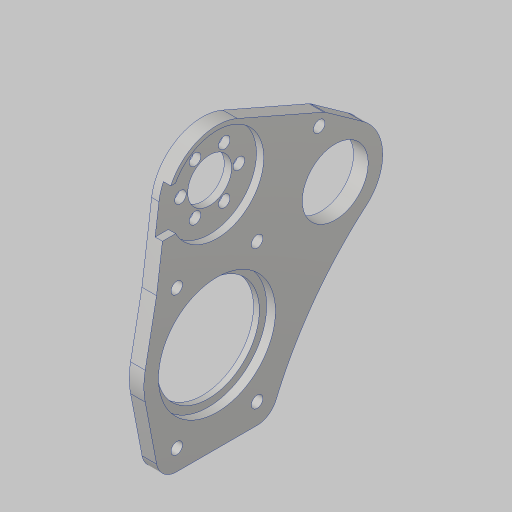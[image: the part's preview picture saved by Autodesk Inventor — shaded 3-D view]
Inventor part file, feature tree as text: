
AUTODESK INVENTOR PART (.ipt)
format: ipt  version: 2023.5 (Build 275446000, 446)  size: 250,880 bytes
history: native  units: in
note: dims shown in document units (in); Inventor stores cm internally (conversion verified against a paired STEP export)
features: sketch x5, extrude x4, hole x2, projected_geometry x1
ambient origin geometry x8: Origin, YZ Plane, XZ Plane, XY Plane, X Axis, Y Axis, Z Axis, Center Point
bodies: Solid1 (feature_tree)
feature tree (12):
  sketch  "Sketch1"  dims[d0=3.0in d1=2.2in]
  sketch  "Sketch2"  dims[d2=3.0in d3=2.375in]
  extrude  "Extrusion1"  Depth=2.2in
  hole  "Motor Mount Holes"  [1 undecoded]
  hole  "Hole3"  [1 undecoded]
  extrude  "Extrusion2"  Depth=0.201in
  extrude  "Extrusion3"  Depth=1.0in
  extrude  "Extrusion4"  Depth=0.875in TaperAngle=360.0deg
  sketch  "Sketch3"  dims[d4=1.375in d5=0.201in]
  sketch  "Sketch4"  dims[d6=0.201in d7=0.201in]
  sketch  "Sketch5"  dims[d8=0.201in d9=1.0in d12=2.3622in d14=360.0deg d16=1.125in d17=2.246in d19=2.0in d20=0.75in d23=0.25in d24=0.25in d25=0.0in d33=0.196in d34=0.75in d35=0.375in d36=0.25in d37=0.5635in d38=1.0in d39=0.8108in d41=1.1811in d43=360.0deg d45=0.375in d46=0.385in d47=0.375in d49=0.196in d50=0.75in d51=0.385in d52=0.25in d53=0.5635in d54=1.0in d55=0.8108in d56=2.0in d57=0.25in d58=1.75in d60=3.0in d61=1.6in d62=0.125in d63=0.0in d65=2.362in d66=0.25in d68=0.75in d69=0.375in d70=0.125in d71=0.0in d72=1.75in d73=0.1in d74=0.0in d75=0.6in d76=2.0in d77=0.875in d78=1.75in]
  projected_geometry  "Project Cut Edges1"
note: 2 required parameter values undecoded (feature->parameter linkage not recoverable at this tier; creation-order binding heuristic only, values carry confidence <= 0.55)
